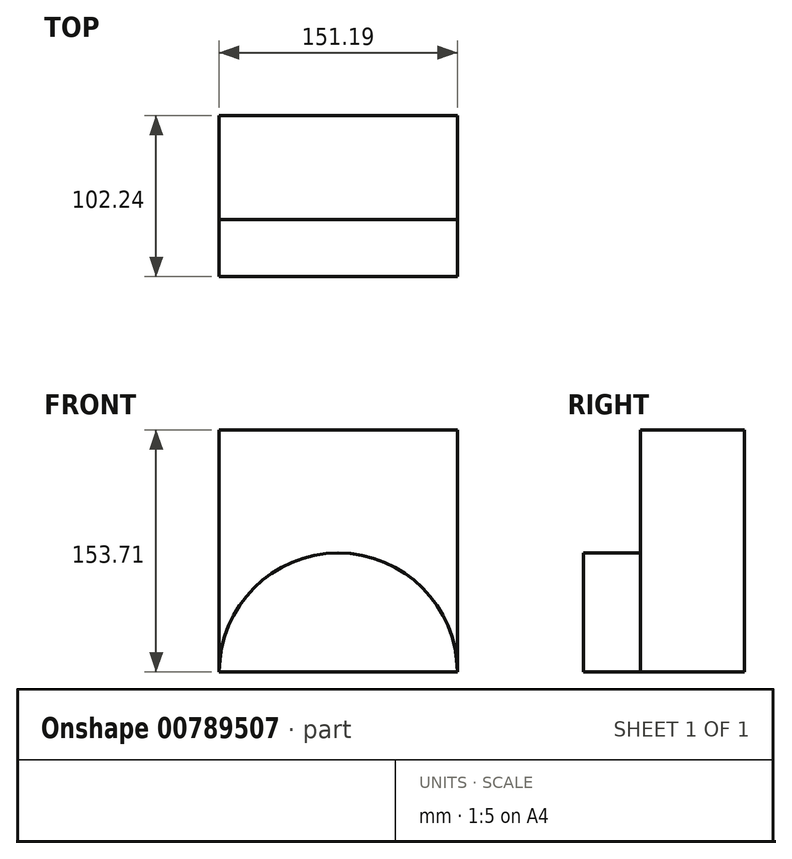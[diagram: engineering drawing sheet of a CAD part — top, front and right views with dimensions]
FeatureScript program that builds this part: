
annotation { "Feature Type Name" : "Feature", "Feature Type Description" : "" }
export const myFeature = defineFeature(function(context is Context, id is Id, definition is map)
    precondition{}
    {
        {
            var Q0;
            Q0=qCreatedBy(makeId("Front.planeOp"),FACE);
            var sketch = newSketch(context, id + "F0", { "sketchPlane" : qUnion([Q0])});
            skLineSegment(sketch, "E0.bottom", {"start": v(74.68, 77.55) * mm, "end": v(-76.5, 77.55) * mm});
            skLineSegment(sketch, "E0.top", {"start": v(74.68, -76.16) * mm, "end": v(-76.5, -76.16) * mm});
            skLineSegment(sketch, "E0.left", {"start": v(74.68, 77.55) * mm, "end": v(74.68, -76.16) * mm});
            skLineSegment(sketch, "E0.right", {"start": v(-76.5, 77.55) * mm, "end": v(-76.5, -76.16) * mm});
            skSolve(sketch);
        }
        {
            var Q0;
            Q0=makeQuery(id+"F0.imprint","IMPRINT",FACE,{"disambiguationData":[TD([[makeQuery(id+"F0.imprint","IMPRINT",EDGE,{"derivedFrom":sQuery(id+"F0.wireOp",EDGE,"E0.bottom")}),1.0]])]});
            extrude(context, id + "F1", {"entities" : qUnion([Q0]), "depth" : 65.92 * mm, "offsetDistance" : 25.4 * mm});
        }
        {
            var Q0;
            Q0=makeQuery(id+"F1.opExtrude","CAP_FACE",FACE,{"disambiguationData":[OSD([sQuery(id+"F0.wireOp",EDGE,"E0.bottom"),sQuery(id+"F0.wireOp",EDGE,"E0.top"),sQuery(id+"F0.wireOp",EDGE,"E0.left"),sQuery(id+"F0.wireOp",EDGE,"E0.right")])],"isStart":false});
            var sketch = newSketch(context, id + "F2", { "sketchPlane" : qUnion([Q0])});
            skArc(sketch, "E1", {"start": v(74.68, -76.16) * mm, "mid": v(-0.91, -0.56) * mm, "end": v(-76.5, -76.16) * mm});
            skSolve(sketch);
        }
        {
            var Q0;
            Q0=makeQuery(id+"F2.imprint","IMPRINT",FACE,{"disambiguationData":[TD([[makeQuery(id+"F2.imprint","IMPRINT",EDGE,{"derivedFrom":sQuery(id+"F2.wireOp",EDGE,"E1")}),1.0]])]});
            extrude(context, id + "F3", {"entities" : qUnion([Q0]), "operationType" : NewBodyOperationType.ADD, "depth" : 36.31 * mm, "offsetDistance" : 25.4 * mm});
        }
    });
